# Revit family: METALFIRE_ULTIMATE_C_MF_WHE_1S
name_source: partatom
category: Mechanical Equipment
revit_build: Autodesk Revit 2017 (Build: 20160225_1515(x64)
units: mm (PartAtom-declared; Revit-internal decimal feet)

## family parameters
Always vertical = Yes
Cut with Voids When Loaded = No
Host = Wall
OmniClass Number = 23.75.00.00
OmniClass Title = Climate Control (HVAC)
Part Type = Normal
Room Calculation Point = Yes
Round Connector Dimension = Use Diameter
Shared = No

## types (1)
- 1300 x 500 mm
    BIM BADGE = https://bim.archiproducts.com
    CO EMISSION = 0.10%
    Description = This generation of room air independent wood fireplaces with liftable door is equipped with a dynamic combustion technique that ensures optimal combustion and high efficiency.
    EFFICIENCY = 70.00%
    ENERGY EFFICIENCY CLASS = A
    FINE DUST EMISSION = 17 mg/Nm3
    FINISHING MATERIAL = Black painted vermiculite plates - Metalfire
    FRAME MATERIAL = Iron - Metalfire
    HEIGHT = 510 mm
    MATERIAL DESCRIPTION = Iron, galvanized steel and vermiculite plates
    Manufacturer = Metalfire
    Model = Ultime C
    OUTPUT = 26.3 kW
    OVERALL DEPTH = 596 mm
    OVERALL HEIGHT = 1360 mm
    OVERALL WIDTH = 1500 mm
    PRODUCT CODE = MF 1300-50 WHE 1S
    PRODUCT SHEET = https://www.archiproducts.com
    SMOKE EXHAUST = Ø250 mm
    TECHNICAL SHEET = https://www.metalfire.eu
    URL = https://www.metalfire.eu
    WEIGHT = 433.00 kg
    WIDTH = 1308 mm

## geometry (parser evidence)
native form markers: Sweep x2
no freeform markers — native parametric forms only
